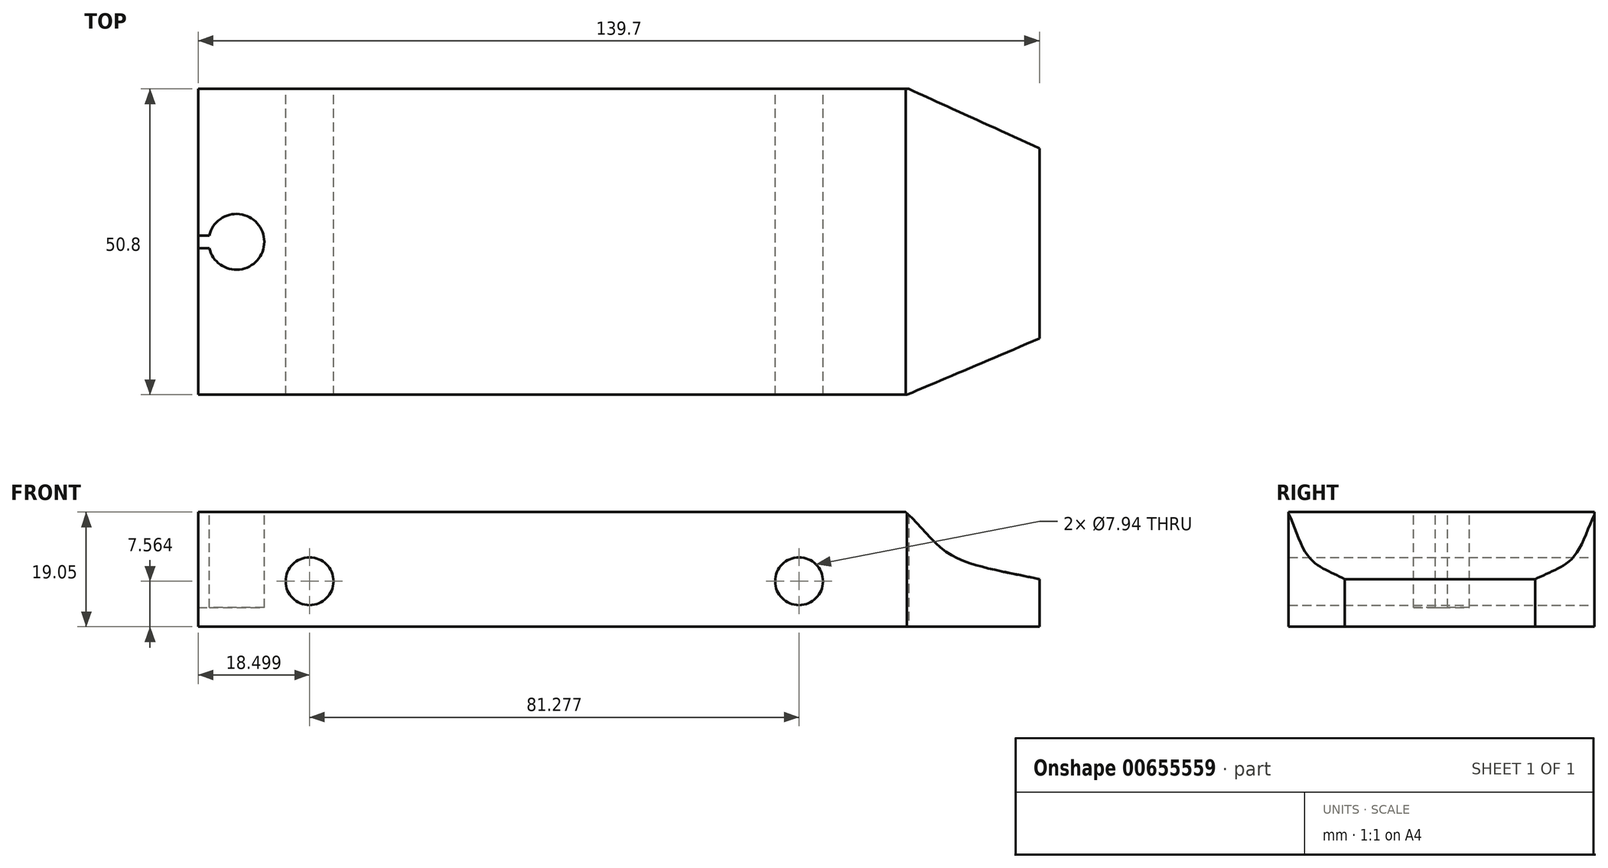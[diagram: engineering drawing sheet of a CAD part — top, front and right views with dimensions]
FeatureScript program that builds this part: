
annotation { "Feature Type Name" : "Feature", "Feature Type Description" : "" }
export const myFeature = defineFeature(function(context is Context, id is Id, definition is map)
    precondition{}
    {
        {
            var Q0;
            Q0=qCreatedBy(makeId("Front.planeOp"),FACE);
            var sketch = newSketch(context, id + "F0", { "sketchPlane" : qUnion([Q0])});
            skLineSegment(sketch, "E0", {"start": v(0, 0) * mm, "end": v(-139.7, 0) * mm});
            skLineSegment(sketch, "E1", {"start": v(-139.7, 0) * mm, "end": v(-139.7, 19.05) * mm});
            skLineSegment(sketch, "E2", {"start": v(-139.7, 19.05) * mm, "end": v(-22.23, 19.05) * mm});
            skLineSegment(sketch, "E3", {"start": v(0, 0) * mm, "end": v(0, 7.9) * mm});
            skFitSpline(sketch, "E4", {"points": [v(-22.23, 19.05) * mm, v(-15.2, 12.27) * mm, v(0, 7.9) * mm], "startDerivative": vector(17.44, -14.77) * mm, "endDerivative": vector(35.16, -7.64) * mm});
            skLineSegment(sketch, "E5", {"start": v(-141.96, 7.56) * mm, "end": v(-16.23, 7.56) * mm, "construction": true});
            skCircle(sketch, "E6", {"center": v(-121.2, 7.56) * mm, "radius": 3.97 * mm});
            skCircle(sketch, "E7", {"center": v(-39.92, 7.56) * mm, "radius": 3.97 * mm});
            skSolve(sketch);
        }
        {
            var Q0;
            Q0=makeQuery(id+"F0.imprint","IMPRINT",FACE,{"disambiguationData":[TD([[makeQuery(id+"F0.imprint","IMPRINT",EDGE,{"derivedFrom":sQuery(id+"F0.wireOp",EDGE,"E0")}),-1.0]])]});
            extrude(context, id + "F1", {"entities" : qUnion([Q0]), "depth" : 50.8 * mm, "offsetDistance" : 25.4 * mm});
        }
        {
            var Q0;
            Q0=makeQuery(id+"F1.opExtrude","SWEPT_FACE",FACE,{"disambiguationData":[OSD([sQuery(id+"F0.wireOp",EDGE,"E2")])]});
            var sketch = newSketch(context, id + "F2", { "sketchPlane" : qUnion([Q0])});
            skPoint(sketch, "E8", {"position": v(-133.35, -25.4) * mm});
            skArc(sketch, "E9", {"start": v(-137.86, -26.44) * mm, "mid": v(-128.72, -25.4) * mm, "end": v(-137.86, -24.36) * mm});
            skLineSegment(sketch, "E10", {"start": v(-139.7, -24.39) * mm, "end": v(-137.86, -24.36) * mm});
            skLineSegment(sketch, "E11", {"start": v(-139.7, -26.44) * mm, "end": v(-137.86, -26.44) * mm});
            skSolve(sketch);
        }
        {
            var Q0;
            Q0=makeQuery(id+"F2.imprint","IMPRINT",FACE,{"disambiguationData":[TD([[makeQuery(id+"F2.imprint","IMPRINT",EDGE,{"derivedFrom":sQuery(id+"F2.wireOp",EDGE,"E9")}),1.0]])]});
            extrude(context, id + "F3", {"entities" : qUnion([Q0]), "operationType" : NewBodyOperationType.REMOVE, "oppositeDirection" : true, "depth" : 15.88 * mm, "offsetDistance" : 25.4 * mm});
        }
        {
            var Q0;
            Q0=makeQuery(id+"F1.opExtrude","SWEPT_FACE",FACE,{"disambiguationData":[OSD([sQuery(id+"F0.wireOp",EDGE,"E2")])]});
            var sketch = newSketch(context, id + "F4", { "sketchPlane" : qUnion([Q0])});
            skLineSegment(sketch, "E12", {"start": v(-22.23, 0) * mm, "end": v(0, -9.46) * mm});
            skLineSegment(sketch, "E13", {"start": v(-22.23, -50.8) * mm, "end": v(0, -43.75) * mm});
            skLineSegment(sketch, "E14", {"start": v(0, -43.75) * mm, "end": v(0, -51.02) * mm});
            skLineSegment(sketch, "E15", {"start": v(0, -51.02) * mm, "end": v(-22.23, -50.8) * mm});
            skLineSegment(sketch, "E16", {"start": v(0, -9.46) * mm, "end": v(0, -43.75) * mm});
            skLineSegment(sketch, "E17", {"start": v(-22.23, -50.8) * mm, "end": v(-139.7, -50.8) * mm});
            skLineSegment(sketch, "E18", {"start": v(-139.7, -50.8) * mm, "end": v(-139.7, 0) * mm});
            skLineSegment(sketch, "E19", {"start": v(-139.7, 0) * mm, "end": v(-22.23, 0) * mm});
            skSolve(sketch);
        }
        {
            var Q0;
            Q0=makeQuery(id+"F1.opExtrude","SWEPT_FACE",FACE,{"disambiguationData":[OSD([sQuery(id+"F0.wireOp",EDGE,"E0")])]});
            var sketch = newSketch(context, id + "F5", { "sketchPlane" : qUnion([Q0])});
            skLineSegment(sketch, "E20", {"start": v(0, 9.66) * mm, "end": v(-22.4, 0) * mm});
            skLineSegment(sketch, "E21", {"start": v(-22.4, 0) * mm, "end": v(0, 0) * mm});
            skLineSegment(sketch, "E22", {"start": v(0, 0) * mm, "end": v(0, 9.66) * mm});
            skLineSegment(sketch, "E23", {"start": v(-21.98, 50.8) * mm, "end": v(0, 50.8) * mm});
            skLineSegment(sketch, "E24", {"start": v(0, 50.8) * mm, "end": v(0, 41.46) * mm});
            skLineSegment(sketch, "E25", {"start": v(0, 41.46) * mm, "end": v(-21.98, 50.8) * mm});
            skSolve(sketch);
        }
        {
            var Q0;
            Q0=makeQuery(id+"F5.imprint","IMPRINT",FACE,{"disambiguationData":[TD([[makeQuery(id+"F5.imprint","IMPRINT",EDGE,{"derivedFrom":sQuery(id+"F5.wireOp",EDGE,"E23")}),1.0]])]});
            extrude(context, id + "F6", {"entities" : qUnion([Q0]), "operationType" : NewBodyOperationType.REMOVE, "oppositeDirection" : true, "depth" : 25.4 * mm, "offsetDistance" : 25.4 * mm});
        }
        {
            var Q0;
            Q0=makeQuery(id+"F1.opExtrude","SWEPT_FACE",FACE,{"disambiguationData":[OSD([sQuery(id+"F0.wireOp",EDGE,"E0")])]});
            var sketch = newSketch(context, id + "F7", { "sketchPlane" : qUnion([Q0])});
            skLineSegment(sketch, "E26", {"start": v(-21.73, 0) * mm, "end": v(0, 9.87) * mm});
            skLineSegment(sketch, "E27", {"start": v(0, 9.87) * mm, "end": v(0, 0) * mm});
            skLineSegment(sketch, "E28", {"start": v(0, 0) * mm, "end": v(-21.73, 0) * mm});
            skSolve(sketch);
        }
        {
            var Q0;
            Q0 = qSketchRegion(id + "F7", true);
            extrude(context, id + "F8", {"entities" : qUnion([Q0]), "operationType" : NewBodyOperationType.REMOVE, "oppositeDirection" : true, "depth" : 25.4 * mm, "offsetDistance" : 25.4 * mm});
        }
    });
